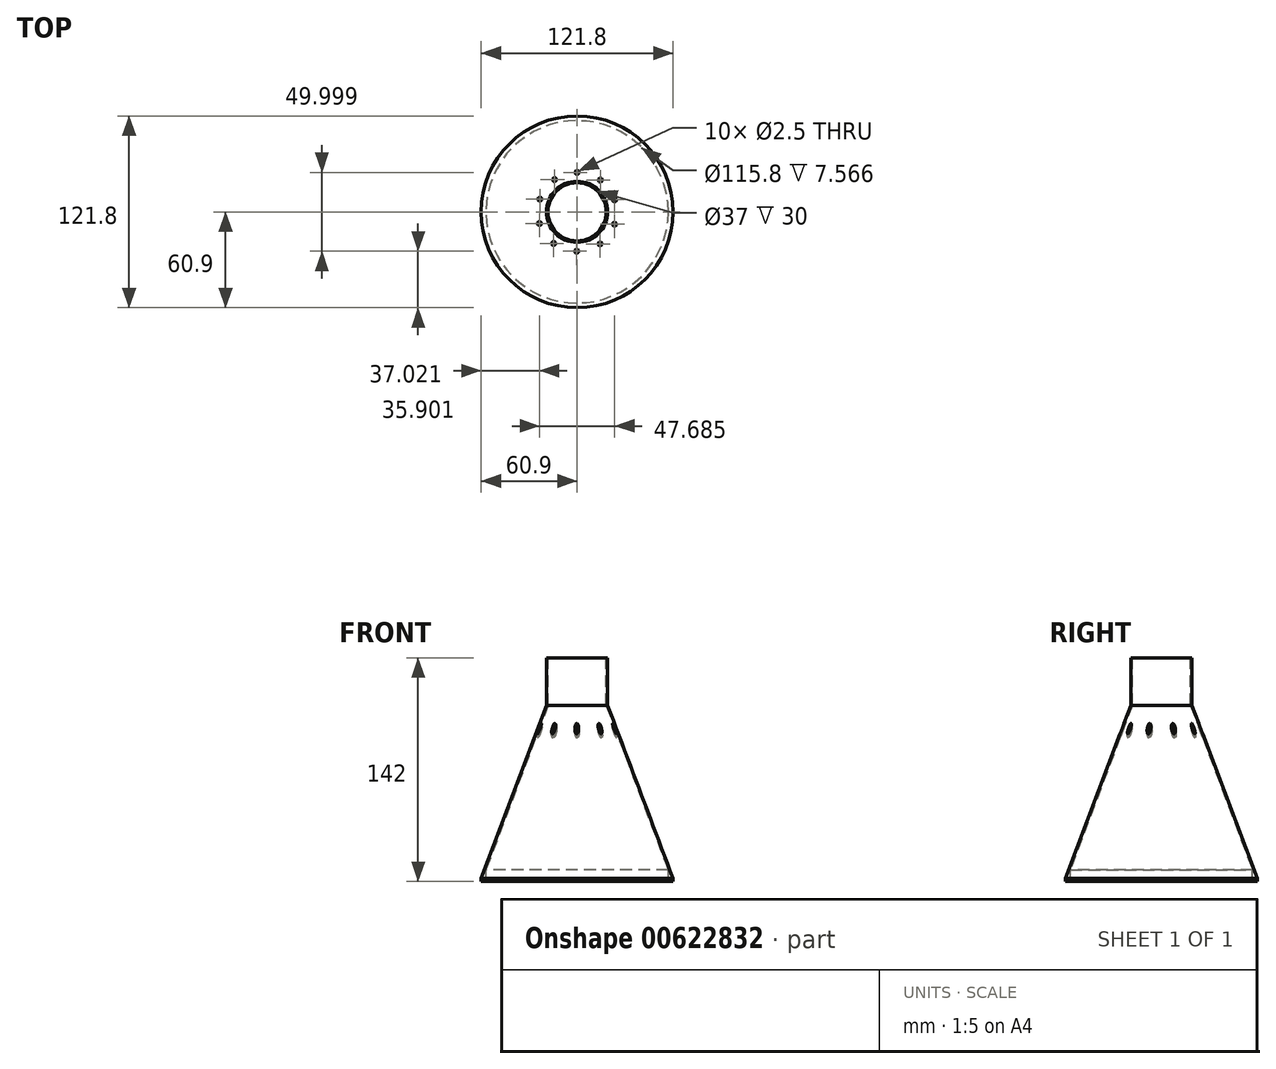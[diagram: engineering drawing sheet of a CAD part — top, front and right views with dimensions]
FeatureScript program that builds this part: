
annotation { "Feature Type Name" : "Feature", "Feature Type Description" : "" }
export const myFeature = defineFeature(function(context is Context, id is Id, definition is map)
    precondition{}
    {
        {
            var Q0;
            Q0=qCreatedBy(makeId("Front.planeOp"),FACE);
            var sketch = newSketch(context, id + "F0", { "sketchPlane" : qUnion([Q0])});
            skLineSegment(sketch, "E0", {"start": v(0, 0) * mm, "end": v(0, 30) * mm, "construction": true});
            skLineSegment(sketch, "E1", {"start": v(0, 30) * mm, "end": v(-18.5, 30) * mm, "construction": true});
            skLineSegment(sketch, "E2", {"start": v(-18.5, 30) * mm, "end": v(-18.5, 0) * mm});
            skLineSegment(sketch, "E3", {"start": v(0, 0) * mm, "end": v(0, -110) * mm, "construction": true});
            skLineSegment(sketch, "E4", {"start": v(0, -110) * mm, "end": v(-60, -110) * mm, "construction": true});
            skLineSegment(sketch, "E5", {"start": v(-18.5, 30) * mm, "end": v(-19.4, 30) * mm});
            skLineSegment(sketch, "E6", {"start": v(-19.4, 30) * mm, "end": v(-19.4, 0) * mm});
            skLineSegment(sketch, "E7", {"start": v(-19.4, 0) * mm, "end": v(-60.9, -110) * mm});
            skLineSegment(sketch, "E8", {"start": v(-60.9, -110) * mm, "end": v(-60, -110) * mm});
            skLineSegment(sketch, "E9", {"start": v(-60.9, -110) * mm, "end": v(-60.9, -112) * mm});
            skLineSegment(sketch, "E10", {"start": v(-60.9, -112) * mm, "end": v(-57.9, -112) * mm});
            skLineSegment(sketch, "E11", {"start": v(-57.9, -112) * mm, "end": v(-57.9, -104.43) * mm});
            skLineSegment(sketch, "E12", {"start": v(-18.5, 0) * mm, "end": v(-57.9, -104.43) * mm});
            skSolve(sketch);
        }
        {
            var Q0;
            Q0 = qSketchRegion(id + "F0", true);
            var Q1;
            Q1=sQuery(id+"F0.wireOp",EDGE,"E3");
            revolve(context, id + "F1", {"entities" : qUnion([Q0]), "axis" : qUnion([Q1]), "revolveType" : RevolveType.FULL});
        }
        {
            var Q0;
            Q0=qCreatedBy(makeId("Top.planeOp"),FACE);
            var sketch = newSketch(context, id + "F2", { "sketchPlane" : qUnion([Q0])});
            skLineSegment(sketch, "E13", {"start": v(0, 0) * mm, "end": v(0, 25) * mm, "construction": true});
            skCircle(sketch, "E14", {"center": v(0, 25) * mm, "radius": 1.25 * mm});
            skCircle(sketch, "E15.1.0", {"center": v(14.73, 20.2) * mm, "radius": 1.25 * mm});
            skCircle(sketch, "E15.2.0", {"center": v(23.8, 7.63) * mm, "radius": 1.25 * mm});
            skCircle(sketch, "E15.3.0", {"center": v(23.73, -7.86) * mm, "radius": 1.25 * mm});
            skCircle(sketch, "E15.4.0", {"center": v(14.54, -20.34) * mm, "radius": 1.25 * mm});
            skCircle(sketch, "E15.5.0", {"center": v(-0.24, -25) * mm, "radius": 1.25 * mm});
            skCircle(sketch, "E15.6.0", {"center": v(-14.93, -20.05) * mm, "radius": 1.25 * mm});
            skCircle(sketch, "E15.7.0", {"center": v(-23.88, -7.4) * mm, "radius": 1.25 * mm});
            skCircle(sketch, "E15.8.0", {"center": v(-23.65, 8.1) * mm, "radius": 1.25 * mm});
            skCircle(sketch, "E15.9.0", {"center": v(-14.34, 20.48) * mm, "radius": 1.25 * mm});
            skPoint(sketch, "E15.center", {"position": v(0, 0) * mm});
            skLineSegment(sketch, "E15.anchor2", {"start": v(0, 0) * mm, "end": v(-14.34, 20.48) * mm, "construction": true});
            skSolve(sketch);
        }
        {
            var Q0;
            Q0 = qSketchRegion(id + "F2", true);
            extrude(context, id + "F3", {"entities" : qUnion([Q0]), "operationType" : NewBodyOperationType.REMOVE, "endBound" : BoundingType.THROUGH_ALL, "oppositeDirection" : true, "depth" : 25 * mm, "offsetDistance" : 25 * mm});
        }
    });
